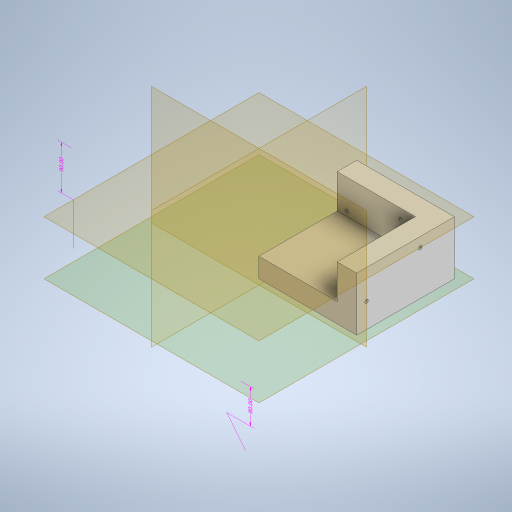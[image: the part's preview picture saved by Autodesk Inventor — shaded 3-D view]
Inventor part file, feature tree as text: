
AUTODESK INVENTOR PART (.ipt)
format: ipt  version: 2023 (Build 270158000, 158)  size: 433,152 bytes
history: native  units: mm
features: sketch x9, extrude x5, other x4, hole x4, plane x4, split x4
ambient origin geometry x8: Origin, YZ Plane, XZ Plane, XY Plane, X Axis, Y Axis, Z Axis, Center Point
bodies: Body1 (feature_tree)
feature tree (30):
  other  "Sólido1"
  other  "Anotaciones"
  extrude  "Extrusión1"  Depth=200.0mm
  hole  "Agujero1"  [1 undecoded]
  extrude  "Extrusión2"  Depth=15.0mm
  extrude  "Extrusión3"  Depth=80.0mm TaperAngle=0.0deg
  extrude  "Extrusión4"  Depth=200.0mm
  extrude  "Extrusión5"  Depth=20.0mm
  hole  "Agujero2"  [1 undecoded]
  plane  "Plano de trabajo1"
  split  "Dividir1"
  plane  "Plano de trabajo2"
  plane  "Plano de trabajo3"
  sketch  "Boceto9"  dims[d37=20.0mm d38=20.0mm]
  plane  "Plano de trabajo4"
  hole  "Agujero3"  [1 undecoded]
  hole  "Agujero4"  [1 undecoded]
  split  "Dividir2"
  split  "Dividir3"
  split  "Dividir4"
  sketch  "Boceto2"  dims[d7=15.0mm d8=200.0mm]
  sketch  "Boceto3"  dims[d9=10.0mm d10=0.0mm]
  sketch  "Boceto4"  dims[d12=1.75mm d13=1.75mm d14=1.75mm d15=1.75mm d16=10.0mm d17=10.0mm d19=30.0mm]
  sketch  "Boceto5"  dims[d20=3.5mm d21=6.0mm d22=4.0mm d23=2.0mm d24=90.0deg d25=8.0mm d26=20.594885mm d27=15.0mm]
  sketch  "Boceto6"  dims[d28=20.0mm d29=80.0mm d30=0.0mm]
  sketch  "Boceto7"  dims[d31=48.0mm d32=200.0mm]
  sketch  "Boceto8"  dims[d33=110.0mm d34=0.0mm d36=20.0mm]
  sketch  "Boceto10"  dims[d39=90.0mm d40=0.0mm d42=10.0mm d43=30.0mm d44=0.0mm d46=1.75mm d47=1.75mm d48=1.75mm d49=1.75mm d50=10.0mm d51=10.0mm d52=15.0mm d56=3.5mm d57=6.0mm d58=4.0mm d59=2.0mm d60=90.0deg d61=8.0mm d62=20.594885mm d63=10.0mm d65=10.0mm d66=10.0mm d67=31.75mm d70=15.0mm d74=200.0mm d78=20.0mm d82=90.0deg d83=10.0mm d84=30.0mm d85=5.0mm d86=5.0mm d87=5.0mm d88=5.0mm d89=20.0mm d91=30.0mm d92=5.0mm d93=5.0mm d94=3.5mm d95=5.0mm d96=5.0mm d97=5.0mm d98=5.0mm d99=5.0mm d100=20.0mm d101=3.5mm d102=6.0mm d103=4.0mm d104=2.0mm d105=90.0deg d106=8.0mm d107=20.594885mm d108=10.0mm d109=30.0mm d110=5.0mm d111=5.0mm d112=5.0mm d113=5.0mm d114=5.0mm d115=5.0mm d116=3.5mm d117=5.0mm d118=5.0mm d119=5.0mm d120=5.0mm d121=5.0mm d122=30.0mm d123=30.0mm d124=3.5mm d125=6.0mm d126=4.0mm d127=2.0mm d128=90.0deg d129=8.0mm d130=20.594885mm d75=1.454734mm d76=6.982969mm d77=80.0mm d79=4.097996mm d80=1.406125mm d81=90.0mm]
  other  "Cota lineal 2"
  other  "Cota lineal 3"
note: 4 required parameter values undecoded (feature->parameter linkage not recoverable at this tier; creation-order binding heuristic only, values carry confidence <= 0.55)
